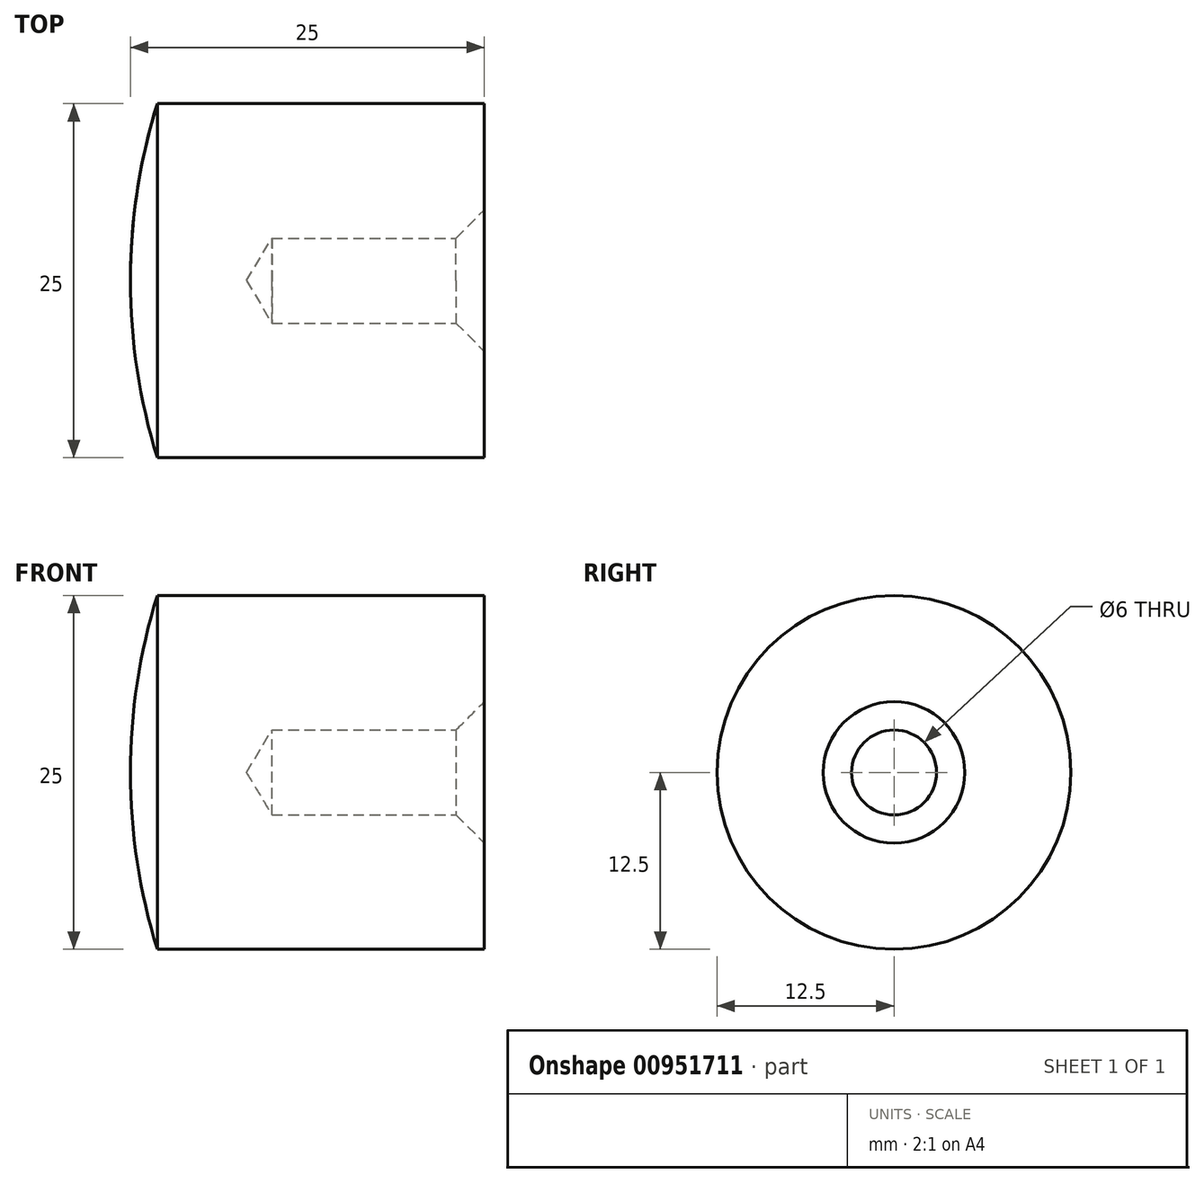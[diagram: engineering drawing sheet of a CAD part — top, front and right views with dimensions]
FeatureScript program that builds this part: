
annotation { "Feature Type Name" : "Feature", "Feature Type Description" : "" }
export const myFeature = defineFeature(function(context is Context, id is Id, definition is map)
    precondition{}
    {
        {
            var Q0;
            Q0=qCreatedBy(makeId("Top.planeOp"),FACE);
            var sketch = newSketch(context, id + "F0", { "sketchPlane" : qUnion([Q0])});
            skLineSegment(sketch, "E0.bottom", {"start": v(-10.69, 12.5) * mm, "end": v(12.41, 12.5) * mm});
            skLineSegment(sketch, "E0.left", {"start": v(-10.69, 12.5) * mm, "end": v(-10.69, 0) * mm});
            skLineSegment(sketch, "E0.right", {"start": v(12.41, 12.5) * mm, "end": v(12.41, 3) * mm});
            skLineSegment(sketch, "E1", {"start": v(-10.69, 0) * mm, "end": v(-12.59, 0) * mm});
            skLineSegment(sketch, "E2", {"start": v(12.41, 3) * mm, "end": v(-2.59, 3) * mm});
            skLineSegment(sketch, "E3", {"start": v(-2.59, 3) * mm, "end": v(-4.4, 0) * mm});
            skLineSegment(sketch, "E4", {"start": v(-4.4, 0) * mm, "end": v(-10.69, 0) * mm});
            skArc(sketch, "E5", {"start": v(-10.69, 12.5) * mm, "mid": v(-12.11, 6.32) * mm, "end": v(-12.59, 0) * mm});
            skSolve(sketch);
        }
        {
            var Q0;
            Q0=makeQuery(id+"F0.imprint","IMPRINT",FACE,{"disambiguationData":[TD([[makeQuery(id+"F0.imprint","IMPRINT",EDGE,{"derivedFrom":sQuery(id+"F0.wireOp",EDGE,"E0.bottom")}),-1.0]])]});
            var Q1;
            Q1=makeQuery(id+"F0.imprint","IMPRINT",FACE,{"disambiguationData":[TD([[makeQuery(id+"F0.imprint","IMPRINT",EDGE,{"derivedFrom":sQuery(id+"F0.wireOp",EDGE,"E0.left")}),-1.0]])]});
            var Q2;
            Q2=sQuery(id+"F0.wireOp",EDGE,"E4");
            revolve(context, id + "F1", {"surfaceOperationType" : NewSurfaceOperationType.NEW, "entities" : qUnion([Q0, Q1]), "axis" : qUnion([Q2]), "revolveType" : RevolveType.FULL});
        }
        {
            var Q0;
            Q0=makeQuery(id+"F1.opRevolve","SWEPT_EDGE",EDGE,{"disambiguationData":[OSD([sQuery(id+"F0.wireOp",EDGE,"E0.right"),sQuery(id+"F0.wireOp",EDGE,"E2")])]});
            chamfer(context, id + "F2", {"entities" : qUnion([Q0]), "width" : 2 * mm, "tangentPropagation" : true});
        }
    });
